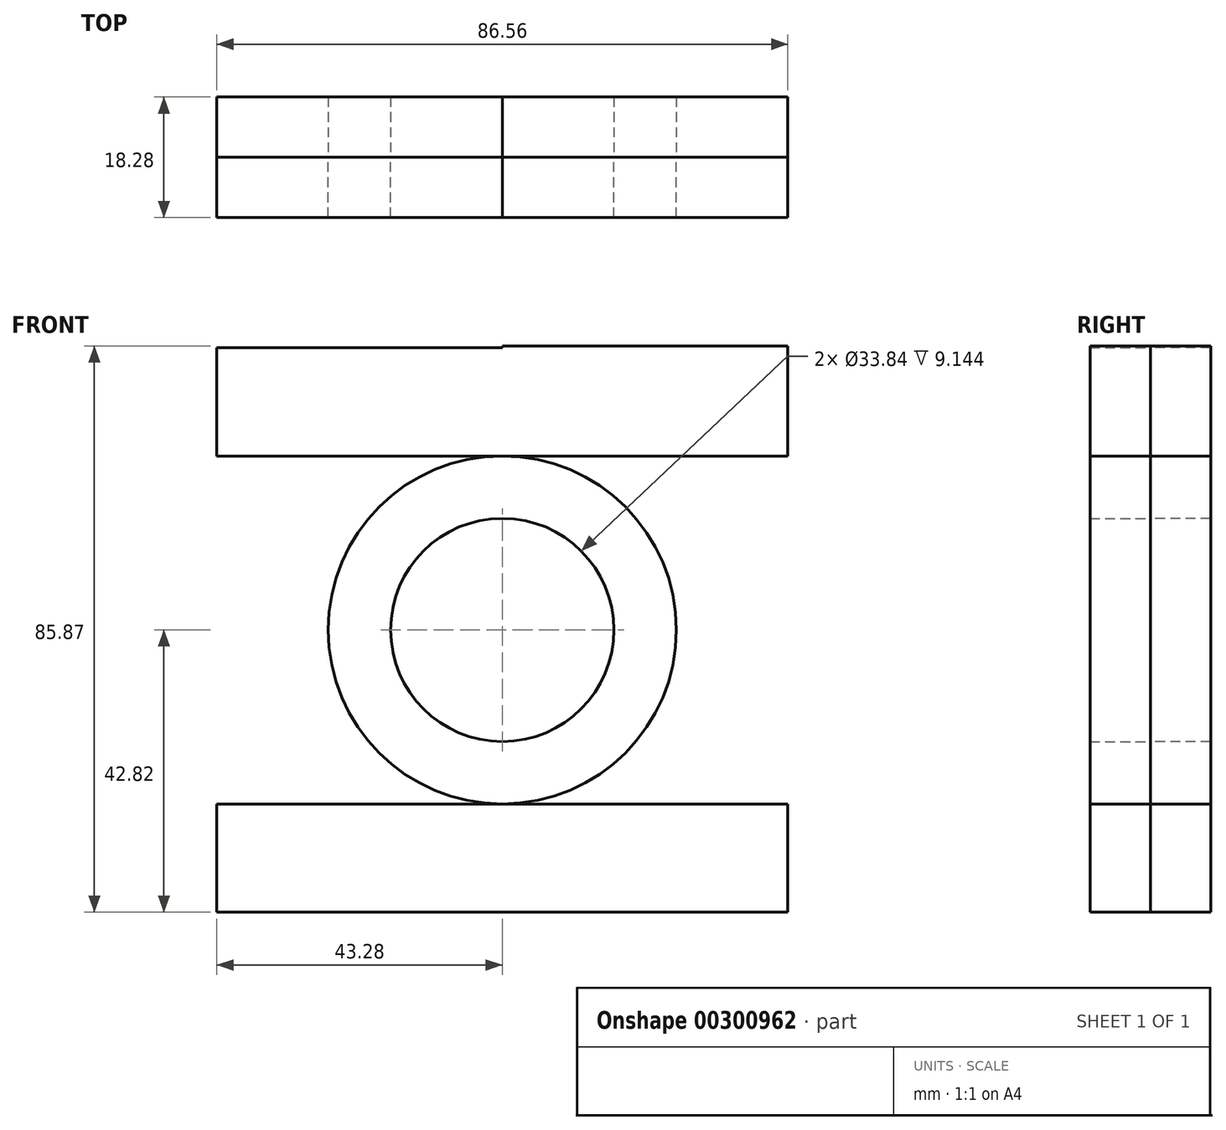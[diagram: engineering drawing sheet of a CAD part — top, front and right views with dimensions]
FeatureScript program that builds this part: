
annotation { "Feature Type Name" : "Feature", "Feature Type Description" : "" }
export const myFeature = defineFeature(function(context is Context, id is Id, definition is map)
    precondition{}
    {
        {
            var Q0;
            Q0=qCreatedBy(makeId("Front.planeOp"),FACE);
            var sketch = newSketch(context, id + "F0", { "sketchPlane" : qUnion([Q0])});
            skCircle(sketch, "E0", {"center": v(0, 0) * mm, "radius": 16.92 * mm});
            skCircle(sketch, "E1", {"center": v(0, 0) * mm, "radius": 26.39 * mm});
            skLineSegment(sketch, "E2.bottom", {"start": v(0, 26.39) * mm, "end": v(-43.28, 26.39) * mm});
            skLineSegment(sketch, "E2.top", {"start": v(0, 42.82) * mm, "end": v(-43.28, 42.82) * mm});
            skLineSegment(sketch, "E2.left", {"start": v(0, 26.39) * mm, "end": v(0, 42.82) * mm});
            skLineSegment(sketch, "E2.right", {"start": v(-43.28, 26.39) * mm, "end": v(-43.28, 42.82) * mm});
            skLineSegment(sketch, "E3.bottom", {"start": v(0, 26.39) * mm, "end": v(43.28, 26.39) * mm});
            skLineSegment(sketch, "E3.top", {"start": v(0, 43.05) * mm, "end": v(43.28, 43.05) * mm});
            skLineSegment(sketch, "E3.left", {"start": v(0, 26.39) * mm, "end": v(0, 43.05) * mm});
            skLineSegment(sketch, "E3.right", {"start": v(43.28, 26.39) * mm, "end": v(43.28, 43.05) * mm});
            skLineSegment(sketch, "E4.bottom", {"start": v(0, -26.39) * mm, "end": v(43.28, -26.39) * mm});
            skLineSegment(sketch, "E4.top", {"start": v(0, -42.82) * mm, "end": v(43.28, -42.82) * mm});
            skLineSegment(sketch, "E4.left", {"start": v(0, -26.39) * mm, "end": v(0, -42.82) * mm});
            skLineSegment(sketch, "E4.right", {"start": v(43.28, -26.39) * mm, "end": v(43.28, -42.82) * mm});
            skLineSegment(sketch, "E5.bottom", {"start": v(0, -42.82) * mm, "end": v(-43.28, -42.82) * mm});
            skLineSegment(sketch, "E5.top", {"start": v(0, -26.39) * mm, "end": v(-43.28, -26.39) * mm});
            skLineSegment(sketch, "E5.left", {"start": v(0, -42.82) * mm, "end": v(0, -26.39) * mm});
            skLineSegment(sketch, "E5.right", {"start": v(-43.28, -42.82) * mm, "end": v(-43.28, -26.39) * mm});
            skSolve(sketch);
        }
        {
            var Q0;
            Q0=makeQuery(id+"F0.imprint","IMPRINT",FACE,{"disambiguationData":[TD([[makeQuery(id+"F0.imprint","IMPRINT",EDGE,{"derivedFrom":sQuery(id+"F0.wireOp",EDGE,"E0")}),-1.0]])]});
            var Q1;
            {var subQ0=sQuery(id+"F0.wireOp",EDGE,"E2.bottom");Q1=makeQuery(id+"F0.imprint","IMPRINT",FACE,{"disambiguationData":[TD([[makeQuery(id+"F0.imprint","IMPRINT",EDGE,{"derivedFrom":subQ0}),-1.0]])]});}
            var Q2;
            {var subQ3=sQuery(id+"F0.wireOp",EDGE,"E3.bottom");Q2=makeQuery(id+"F0.imprint","IMPRINT",FACE,{"disambiguationData":[TD([[makeQuery(id+"F0.imprint","IMPRINT",EDGE,{"derivedFrom":subQ3}),1.0]])]});}
            var Q3;
            Q3=makeQuery(id+"F0.imprint","IMPRINT",FACE,{"disambiguationData":[TD([[makeQuery(id+"F0.imprint","IMPRINT",EDGE,{"derivedFrom":sQuery(id+"F0.wireOp",EDGE,"E5.bottom")}),-1.0]])]});
            var Q4;
            Q4=makeQuery(id+"F0.imprint","IMPRINT",FACE,{"disambiguationData":[TD([[makeQuery(id+"F0.imprint","IMPRINT",EDGE,{"derivedFrom":sQuery(id+"F0.wireOp",EDGE,"E4.bottom")}),-1.0]])]});
            extrude(context, id + "F1", {"entities" : qUnion([Q0, Q1, Q2, Q3, Q4]), "depth" : 9.14 * mm});
        }
        {
            var Q0;
            Q0=makeQuery(id+"F1.opExtrude","CAP_FACE",FACE,{"disambiguationData":[OSD([sQuery(id+"F0.wireOp",EDGE,"E0"),sQuery(id+"F0.wireOp",EDGE,"E1")])],"isStart":true});
            var Q1;
            Q1=makeQuery(id+"F1.opExtrude","CAP_FACE",FACE,{"disambiguationData":[OSD([sQuery(id+"F0.wireOp",EDGE,"E4.bottom"),sQuery(id+"F0.wireOp",EDGE,"E4.top"),sQuery(id+"F0.wireOp",EDGE,"E4.right"),sQuery(id+"F0.wireOp",EDGE,"E5.bottom"),sQuery(id+"F0.wireOp",EDGE,"E5.top"),sQuery(id+"F0.wireOp",EDGE,"E5.right")])],"isStart":true});
            var Q2;
            Q2=makeQuery(id+"F1.opExtrude","CAP_FACE",FACE,{"disambiguationData":[OSD([sQuery(id+"F0.wireOp",EDGE,"E2.bottom"),sQuery(id+"F0.wireOp",EDGE,"E2.top"),sQuery(id+"F0.wireOp",EDGE,"E2.right"),sQuery(id+"F0.wireOp",EDGE,"E3.bottom"),sQuery(id+"F0.wireOp",EDGE,"E3.top"),sQuery(id+"F0.wireOp",EDGE,"E3.left"),sQuery(id+"F0.wireOp",EDGE,"E3.right")])],"isStart":true});
            extrude(context, id + "F2", {"entities" : qUnion([Q0, Q1, Q2]), "depth" : 9.14 * mm});
        }
    });
